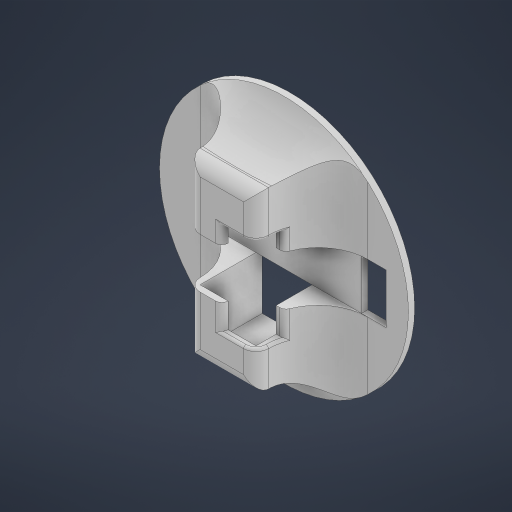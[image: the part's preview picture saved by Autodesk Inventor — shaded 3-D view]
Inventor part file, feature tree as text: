
AUTODESK INVENTOR PART (.ipt)
format: ipt  version: 2023 (Build 270158000, 158)  size: 401,920 bytes
history: native  units: mm
features: extrude x6, sketch x6, fillet x5
ambient origin geometry x8: Origin, YZ Plane, XZ Plane, XY Plane, X Axis, Y Axis, Z Axis, Center Point
bodies: Solid1 (feature_tree)
feature tree (17):
  extrude  "Extrusion1"  Depth=5.0mm TaperAngle=0.0deg
  extrude  "Extrusion2"  Depth=45.0mm
  extrude  "Extrusion3"  Depth=45.0mm
  fillet  "Fillet1"  Radius=40.0mm
  fillet  "Fillet2"  Radius=5.0mm
  extrude  "Extrusion4"  Depth=50.0mm TaperAngle=0.0deg
  extrude  "Extrusion5"  TaperAngle=90.0deg  [1 undecoded]
  fillet  "Fillet3"  Radius=22.5mm
  fillet  "Fillet4"  Radius=45.0mm
  fillet  "Fillet5"  Radius=45.0mm
  extrude  "Extrusion6"  Depth=50.0mm TaperAngle=0.0deg
  sketch  "Sketch1"  dims[d0=200.0mm d1=5.0mm d2=0.0mm]
  sketch  "Sketch2"  dims[d5=22.5mm d6=45.0mm]
  sketch  "Sketch3"  dims[d7=40.0mm d8=45.0mm d9=40.0mm d12=5.0mm]
  sketch  "Sketch4"  dims[d13=5.0mm d14=50.0mm d15=0.0mm]
  sketch  "Sketch5"  dims[d16=20.0mm d17=90.0deg d18=22.5mm d19=45.0mm d20=45.0mm]
  sketch  "Sketch6"  dims[d21=45.0mm d22=50.0mm d23=0.0mm d24=40.0mm d25=10.0mm d26=75.0mm d27=9.0mm d28=0.0mm d29=9.0mm d30=0.0mm d31=5.0mm d32=5.0mm d33=2.0mm d34=9.0mm d35=0.0mm]
note: 1 required parameter value undecoded (feature->parameter linkage not recoverable at this tier; creation-order binding heuristic only, values carry confidence <= 0.55)
